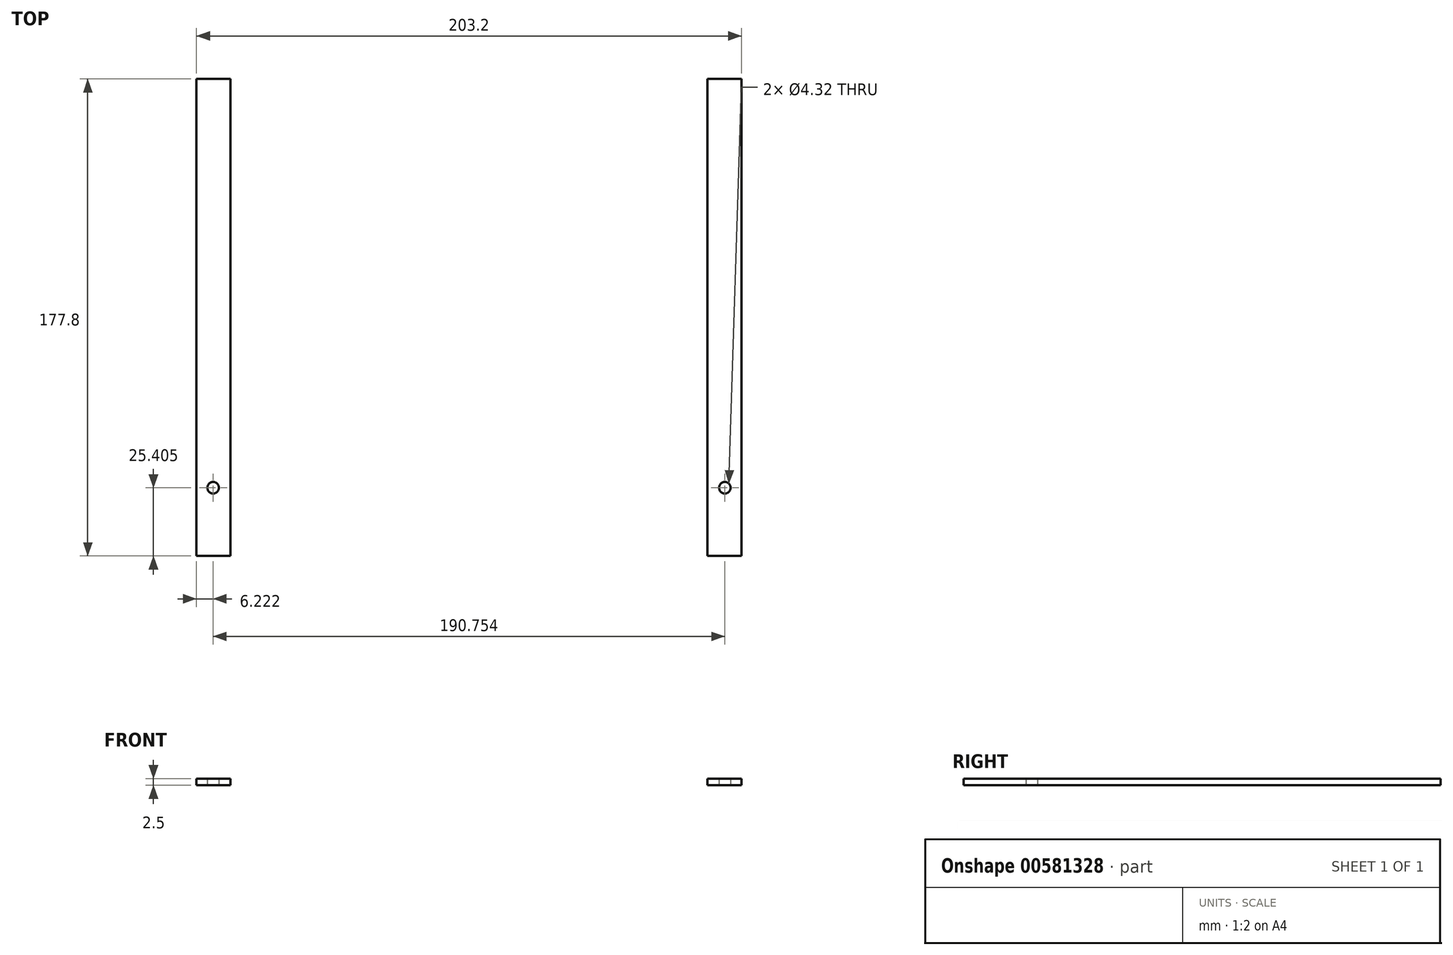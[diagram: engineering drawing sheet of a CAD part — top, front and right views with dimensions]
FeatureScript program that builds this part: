
annotation { "Feature Type Name" : "Feature", "Feature Type Description" : "" }
export const myFeature = defineFeature(function(context is Context, id is Id, definition is map)
    precondition{}
    {
        {
            var Q0;
            Q0=qCreatedBy(makeId("Top.planeOp"),FACE);
            var sketch = newSketch(context, id + "F0", { "sketchPlane" : qUnion([Q0])});
            skLineSegment(sketch, "E0.bottom", {"start": v(94.14, -80.9) * mm, "end": v(-83.66, -80.9) * mm});
            skLineSegment(sketch, "E0.top", {"start": v(94.14, 96.9) * mm, "end": v(-83.66, 96.9) * mm});
            skLineSegment(sketch, "E0.left", {"start": v(94.14, -80.9) * mm, "end": v(94.14, 96.9) * mm});
            skLineSegment(sketch, "E0.right", {"start": v(-83.66, -80.9) * mm, "end": v(-83.66, 96.9) * mm});
            skLineSegment(sketch, "E1.bottom", {"start": v(94.14, 96.9) * mm, "end": v(106.84, 96.9) * mm});
            skLineSegment(sketch, "E1.top", {"start": v(94.14, -80.9) * mm, "end": v(106.84, -80.9) * mm});
            skLineSegment(sketch, "E1.left", {"start": v(94.14, 96.9) * mm, "end": v(94.14, -80.9) * mm});
            skLineSegment(sketch, "E1.right", {"start": v(106.84, 96.9) * mm, "end": v(106.84, -80.9) * mm});
            skLineSegment(sketch, "E2.bottom", {"start": v(-83.66, 96.9) * mm, "end": v(-96.36, 96.9) * mm});
            skLineSegment(sketch, "E2.top", {"start": v(-83.66, -80.9) * mm, "end": v(-96.36, -80.9) * mm});
            skLineSegment(sketch, "E2.left", {"start": v(-83.66, 96.9) * mm, "end": v(-83.66, -80.9) * mm});
            skLineSegment(sketch, "E2.right", {"start": v(-96.36, 96.9) * mm, "end": v(-96.36, -80.9) * mm});
            skLineSegment(sketch, "E3.bottom", {"start": v(-83.66, -80.9) * mm, "end": v(94.14, -80.9) * mm});
            skLineSegment(sketch, "E3.top", {"start": v(-83.66, -93.6) * mm, "end": v(94.14, -93.6) * mm});
            skLineSegment(sketch, "E3.left", {"start": v(-83.66, -80.9) * mm, "end": v(-83.66, -93.6) * mm});
            skLineSegment(sketch, "E3.right", {"start": v(94.14, -80.9) * mm, "end": v(94.14, -93.6) * mm});
            skLineSegment(sketch, "E4.bottom", {"start": v(-83.66, 96.9) * mm, "end": v(94.14, 96.9) * mm});
            skLineSegment(sketch, "E4.top", {"start": v(-83.66, 109.6) * mm, "end": v(94.14, 109.6) * mm});
            skLineSegment(sketch, "E4.left", {"start": v(-83.66, 96.9) * mm, "end": v(-83.66, 109.6) * mm});
            skLineSegment(sketch, "E4.right", {"start": v(94.14, 96.9) * mm, "end": v(94.14, 109.6) * mm});
            skCircle(sketch, "E5", {"center": v(-90.14, -55.5) * mm, "radius": 2.16 * mm});
            skCircle(sketch, "E6", {"center": v(100.62, -55.5) * mm, "radius": 2.16 * mm});
            skCircle(sketch, "E7", {"center": v(61.12, 62.61) * mm, "radius": 3.37 * mm});
            skCircle(sketch, "E8", {"center": v(-50.64, 62.61) * mm, "radius": 3.37 * mm});
            skCircle(sketch, "E9", {"center": v(73.82, -48.76) * mm, "radius": 1.65 * mm});
            skCircle(sketch, "E10", {"center": v(73.82, -62.23) * mm, "radius": 1.65 * mm});
            skCircle(sketch, "E11", {"center": v(83.98, -48.76) * mm, "radius": 1.65 * mm});
            skCircle(sketch, "E12", {"center": v(83.98, -62.23) * mm, "radius": 1.65 * mm});
            skPoint(sketch, "E13", {"position": v(83.98, -55.5) * mm});
            skCircle(sketch, "E14", {"center": v(-73.5, -48.76) * mm, "radius": 1.65 * mm});
            skCircle(sketch, "E15", {"center": v(-73.5, -62.23) * mm, "radius": 1.65 * mm});
            skCircle(sketch, "E16", {"center": v(-63.34, -48.76) * mm, "radius": 1.65 * mm});
            skCircle(sketch, "E17", {"center": v(-63.34, -62.23) * mm, "radius": 1.65 * mm});
            skPoint(sketch, "E18", {"position": v(-63.34, -55.5) * mm});
            skSolve(sketch);
        }
        {
            var Q0;
            Q0=makeQuery(id+"F0.imprint","IMPRINT",FACE,{"disambiguationData":[TD([[makeQuery(id+"F0.imprint","IMPRINT",EDGE,{"derivedFrom":sQuery(id+"F0.wireOp",EDGE,"E3.bottom")}),-1.0]])]});
            var Q1;
            Q1=makeQuery(id+"F0.imprint","IMPRINT",FACE,{"disambiguationData":[TD([[makeQuery(id+"F0.imprint","IMPRINT",EDGE,{"derivedFrom":sQuery(id+"F0.wireOp",EDGE,"E4.bottom")}),1.0]])]});
            var Q2;
            Q2=makeQuery(id+"F0.imprint","IMPRINT",FACE,{"disambiguationData":[TD([[makeQuery(id+"F0.imprint","IMPRINT",EDGE,{"derivedFrom":sQuery(id+"F0.wireOp",EDGE,"E1.bottom")}),-1.0]])]});
            var Q3;
            Q3=makeQuery(id+"F0.imprint","IMPRINT",FACE,{"disambiguationData":[TD([[makeQuery(id+"F0.imprint","IMPRINT",EDGE,{"derivedFrom":sQuery(id+"F0.wireOp",EDGE,"E2.bottom")}),1.0]])]});
            var Q4;
            Q4=makeQuery(id+"F0.imprint","IMPRINT",FACE,{"disambiguationData":[TD([[makeQuery(id+"F0.imprint","IMPRINT",EDGE,{"derivedFrom":sQuery(id+"F0.wireOp",EDGE,"E1.left")}),-1.0]])]});
            extrude(context, id + "F1", {"entities" : qUnion([Q0, Q1, Q2, Q3, Q4]), "depth" : 2.5 * mm, "offsetDistance" : 25 * mm});
        }
    });
